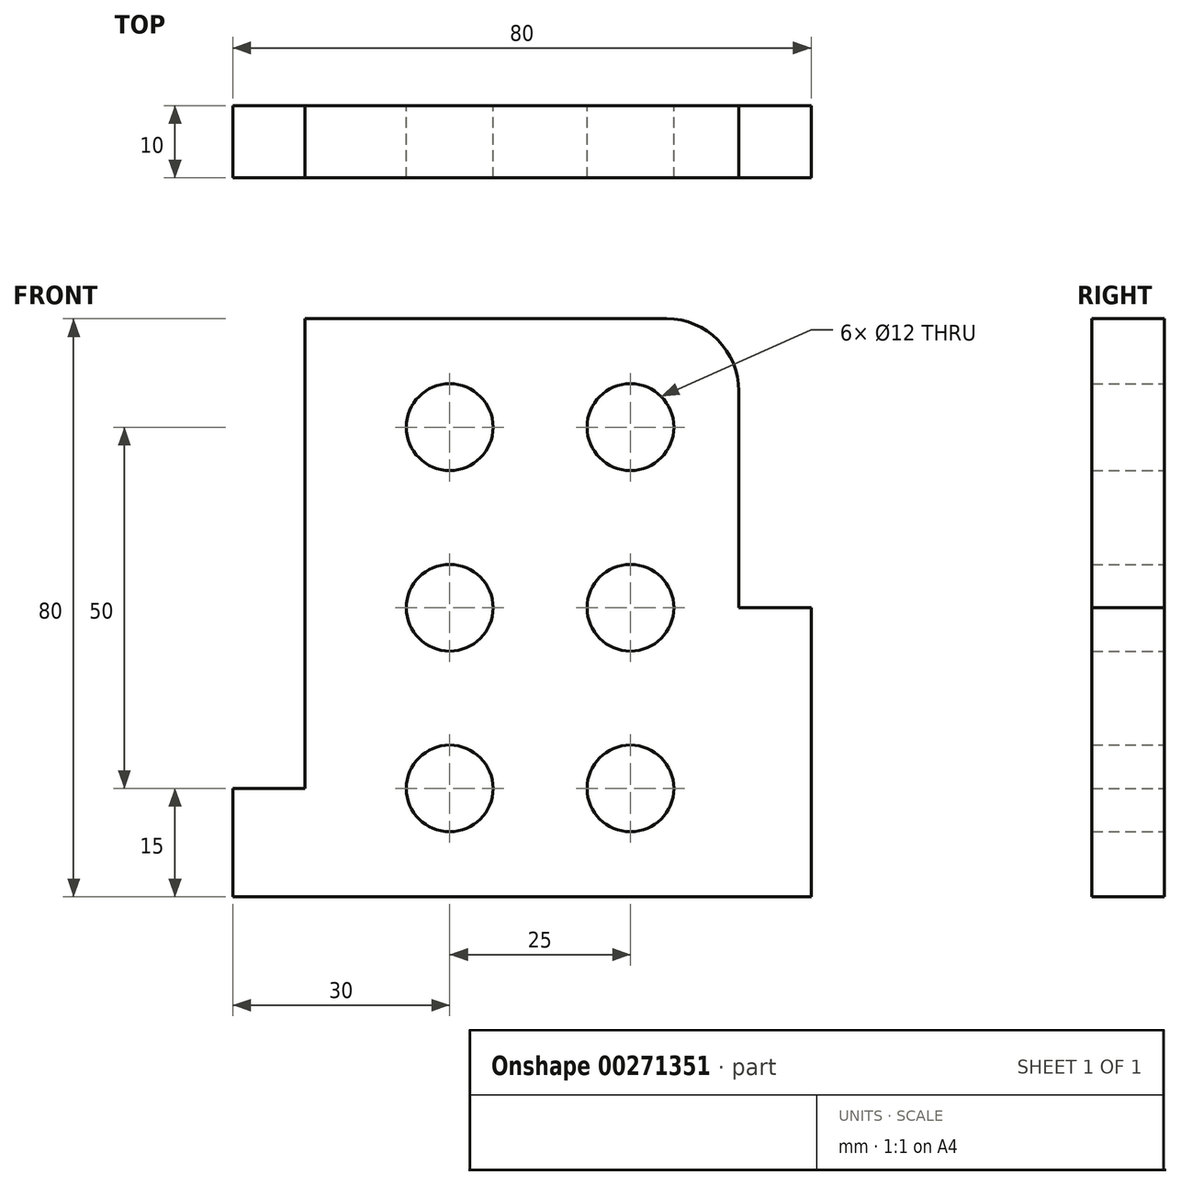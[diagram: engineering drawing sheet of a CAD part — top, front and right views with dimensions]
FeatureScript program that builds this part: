
annotation { "Feature Type Name" : "Feature", "Feature Type Description" : "" }
export const myFeature = defineFeature(function(context is Context, id is Id, definition is map)
    precondition{}
    {
        {
            var Q0;
            Q0=qCreatedBy(makeId("Front.planeOp"),FACE);
            var sketch = newSketch(context, id + "F0", { "sketchPlane" : qUnion([Q0])});
            skLineSegment(sketch, "E0", {"start": v(0, 0) * mm, "end": v(0, 15) * mm});
            skLineSegment(sketch, "E1", {"start": v(0, 15) * mm, "end": v(10, 15) * mm});
            skLineSegment(sketch, "E2", {"start": v(10, 15) * mm, "end": v(10, 80) * mm});
            skLineSegment(sketch, "E3", {"start": v(10, 80) * mm, "end": v(60, 80) * mm});
            skLineSegment(sketch, "E4", {"start": v(70, 70) * mm, "end": v(70, 40) * mm});
            skLineSegment(sketch, "E5", {"start": v(70, 40) * mm, "end": v(80, 40) * mm});
            skLineSegment(sketch, "E6", {"start": v(80, 40) * mm, "end": v(80, 0) * mm});
            skLineSegment(sketch, "E7", {"start": v(80, 0) * mm, "end": v(0, 0) * mm});
            skArc(sketch, "E8", {"start": v(70, 70) * mm, "mid": v(67.07, 77.07) * mm, "end": v(60, 80) * mm});
            skCircle(sketch, "E9", {"center": v(30, 65) * mm, "radius": 6 * mm});
            skCircle(sketch, "E10", {"center": v(55, 65) * mm, "radius": 6 * mm});
            skCircle(sketch, "E11", {"center": v(30, 40) * mm, "radius": 6 * mm});
            skCircle(sketch, "E12", {"center": v(55, 40) * mm, "radius": 6 * mm});
            skCircle(sketch, "E13", {"center": v(30, 15) * mm, "radius": 6 * mm});
            skCircle(sketch, "E14", {"center": v(55, 15) * mm, "radius": 6 * mm});
            skSolve(sketch);
        }
        {
            var Q0;
            Q0=makeQuery(id+"F0.imprint","IMPRINT",FACE,{"disambiguationData":[TD([[makeQuery(id+"F0.imprint","IMPRINT",EDGE,{"derivedFrom":sQuery(id+"F0.wireOp",EDGE,"E0")}),-1.0]])]});
            extrude(context, id + "F1", {"entities" : qUnion([Q0]), "depth" : 10 * mm});
        }
    });
